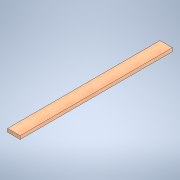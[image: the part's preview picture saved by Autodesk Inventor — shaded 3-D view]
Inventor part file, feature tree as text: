
AUTODESK INVENTOR PART (.ipt)
format: ipt  version: 2020.2 (Build 242310000, 310)  size: 101,376 bytes
history: native  units: in
note: dims shown in document units (in); Inventor stores cm internally (conversion verified against a paired STEP export)
features: extrude x1, sketch x1
ambient origin geometry x8: Origin, YZ Plane, XZ Plane, XY Plane, X Axis, Y Axis, Z Axis, Center Point
bodies: Solid1 (feature_tree)
feature tree (2):
  extrude  "Extrusion1"  Depth=1.5in
  sketch  "Sketch1"  dims[d0=5.5in d1=1.5in d2=67.0in d3=0.0in]
